# Revit family: Diverter_Valve-American_Standard-T342430
name_source: partatom
category: Plumbing Fixtures
units: mm (PartAtom-declared; Revit-internal decimal feet)

## family parameters
Cut with Voids When Loaded = No
Host = Face
OmniClass Number = 23.45.05.14.17
OmniClass Title = Showers
Part Type = Normal
Room Calculation Point = No
Round Connector Dimension = Use Radius
Shared = Yes

## types (1)
- T342.430
    ADA Compliant = Yes
    Assembly Code = D2010710
    CW Connection = Yes
    CWFU = 3
    Cold Water Connection Diameter = 1/2"
    Cold Water Connection Radius = 1/4"
    Default Elevation = 46"
    Description = Heritage Diverter Handle
    HW Connection = Yes
    HWFU = 3
    Height = 2 1/8"
    Hot Water Connection Diameter = 1/2"
    Hot Water Connection Radius = 1/4"
    Installation Type = Wall Mounted
    Length = 2 1/8"
    Manufacturer = American Standard
    Material = <By Category>
    Model = T342.430
    Price = Prices may vary. Please consult Manufacturer Representative for most up-to-date price list.
    URL = http://www.americanstandard-us.com
    Valve Specification = American Standard R422.000 2-Way In-Wall Diverter valve body (Discrete), 1/2" NPT Inlets/Outlets. 2 Discrete functions. LESS Handle. Two way diverter shall feature a forged brass body with 1/2” NPT mixed water inlet and outlets.
    Vent Connection = No
    WFU = 4
    Warranty Information = 1 Year Limited
    Waste Connection = No
    Width = 2 5/8"

## geometry (parser evidence)
native form markers: Sweep x3
no freeform markers — native parametric forms only
